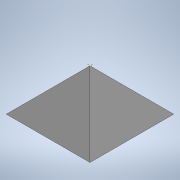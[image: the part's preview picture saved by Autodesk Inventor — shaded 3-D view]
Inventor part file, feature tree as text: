
AUTODESK INVENTOR PART (.ipt)
format: ipt  version: 2020 (Build 240168000, 168)  size: 126,464 bytes
history: native  units: in
note: dims shown in document units (in); Inventor stores cm internally (conversion verified against a paired STEP export)
features: sketch x6, extrude x5, plane x4
ambient origin geometry x8: Origin, YZ Plane, XZ Plane, XY Plane, X Axis, Y Axis, Z Axis, Center Point
bodies: Solid1 (feature_tree)
feature tree (15):
  extrude  "Extrusion1"  Depth=0.5906in
  sketch  "Sketch2"  dims[d2=0.2953in d3=0.0in]
  plane  "Work Plane1"
  plane  "Work Plane2"
  plane  "Work Plane3"
  plane  "Work Plane4"
  extrude  "Extrusion2"  TaperAngle=0.0deg  [1 undecoded]
  extrude  "Extrusion3"  Depth=0.1033in TaperAngle=0.0deg
  extrude  "Extrusion4"  TaperAngle=0.0deg  [1 undecoded]
  extrude  "Extrusion5"  [1 undecoded]
  sketch  "Sketch1"  dims[d0=0.5906in d1=0.5906in]
  sketch  "Sketch4"  dims[d4=0.1264in d5=0.0in d6=0.1033in d7=0.0in]
  sketch  "Sketch5"  dims[d8=0.5906in d9=0.0in]
  sketch  "Sketch6"  dims[d10=0.0508in d11=0.0in]
  sketch  "Sketch7"
note: 3 required parameter values undecoded (feature->parameter linkage not recoverable at this tier; creation-order binding heuristic only, values carry confidence <= 0.55)
